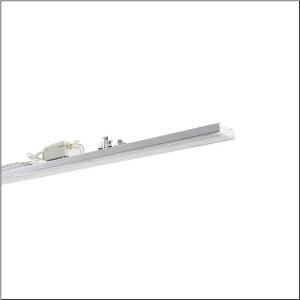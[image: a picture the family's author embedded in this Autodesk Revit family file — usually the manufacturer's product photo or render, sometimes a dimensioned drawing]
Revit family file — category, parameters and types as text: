
# Revit family: licross_r__21_recessed_ho_52te12dn4fxm_2e24
name_source: partatom
category: Lighting Fixtures
units: mm (PartAtom-declared; Revit-internal decimal feet)

## family parameters
Cut with Voids When Loaded = No
Host = Face
Light Source = No
Part Type = Normal
Room Calculation Point = No
Round Connector Dimension = Use Diameter
Shared = No

## types (1)
- --- (1 x LED, 15000 lm, 84.6 W, 4000K)
    Apparent Load = 85 VA
    CIE Flux Codes = 69 91 98 100 100
    Color Rendering = 80
    Color Temperature = 4000K
    Default Elevation = 1800 mm
    Description = Licross® 21 Recessed HO, luminaire insert, of sheet steel, galvanised, coil coated, white, length: 1.500mm, width: 66mm, height: 67mm, LED rated luminous flux: 15.000lm, light colour: 840, control gear: DALI 2, with plug, 5-pole, with phase selection, mains connection: 220..240V, AC, 50/60Hz, rated input power: 85W, halogen-free wiring, primary optical cover: cover, of PMMA, light emission: direct distribution, primary light characteristic: symmetric, protection rating (complete): IP54, insulation class (complete): insulation class I (protective earthing), certification: CE, ENEC, VDE, UKCA, protection symbol: D if used in an environment with non-conductive dust loads with corresponding accessories, impact resistance: IK06, permissible ambient temperature for indoor applications: -25..+30°C, corresponds to IFS (International Featured Standards) requirements for safety and quality in the food industry, reducing of maximum allowable ambient temperature of 5°C with ceiling mounting, LABS conformity tested according to VDMA 24364:2018-05, packaging unit: 1 piece
    Height = 58 mm
    Lamp = 1 x LED
    Lamp Light Flux = 15000 lm
    Lamp Power = 84.6 W
    Lamp count = 1
    Length = 1500 mm
    Luminous efficacy = 177 lm/W
    Manufacturer = Siteco
    ModVariant = No
    Model = 52TE12DN4FXM
    Mounting Place = Ceiling
    Mounting Type = Pendant
    Number of Poles = 1
    OnlyDefault = Yes
    Power Factor = 1
    Product Name = Licross® 21 Recessed HO
    Product group = luminaire insert
    ProductGroupID = 901
    Protection Class = Protection class I
    Protection Degree = IP 54
    RLX_Detail_Level = 1
    RLX_Emergency_Light_Flux = 0 lm
    RLX_Emergency_Type = 0
    RLX_Emergency_Type_DB = No
    RlxData = <blob elided: 24741 chars, md5=003921be>
    Socket = socket
    Standby Power = 0 W
    System Light Flux = 15000 lm
    System Power = 85 W
    Type Comments = factory setting: luminous flux: 100 % | dim-lin: 254 | 484 mA
    Type Image = l_1296930.jpg
    URL = http://relux.com
    VarID = @adj_046473
    Voltage = 0 V
    Weight = 0.00 kg
    Width = 66 mm

## geometry (parser evidence)
native form markers: Blend x4, Sweep x10
no freeform markers — native parametric forms only
